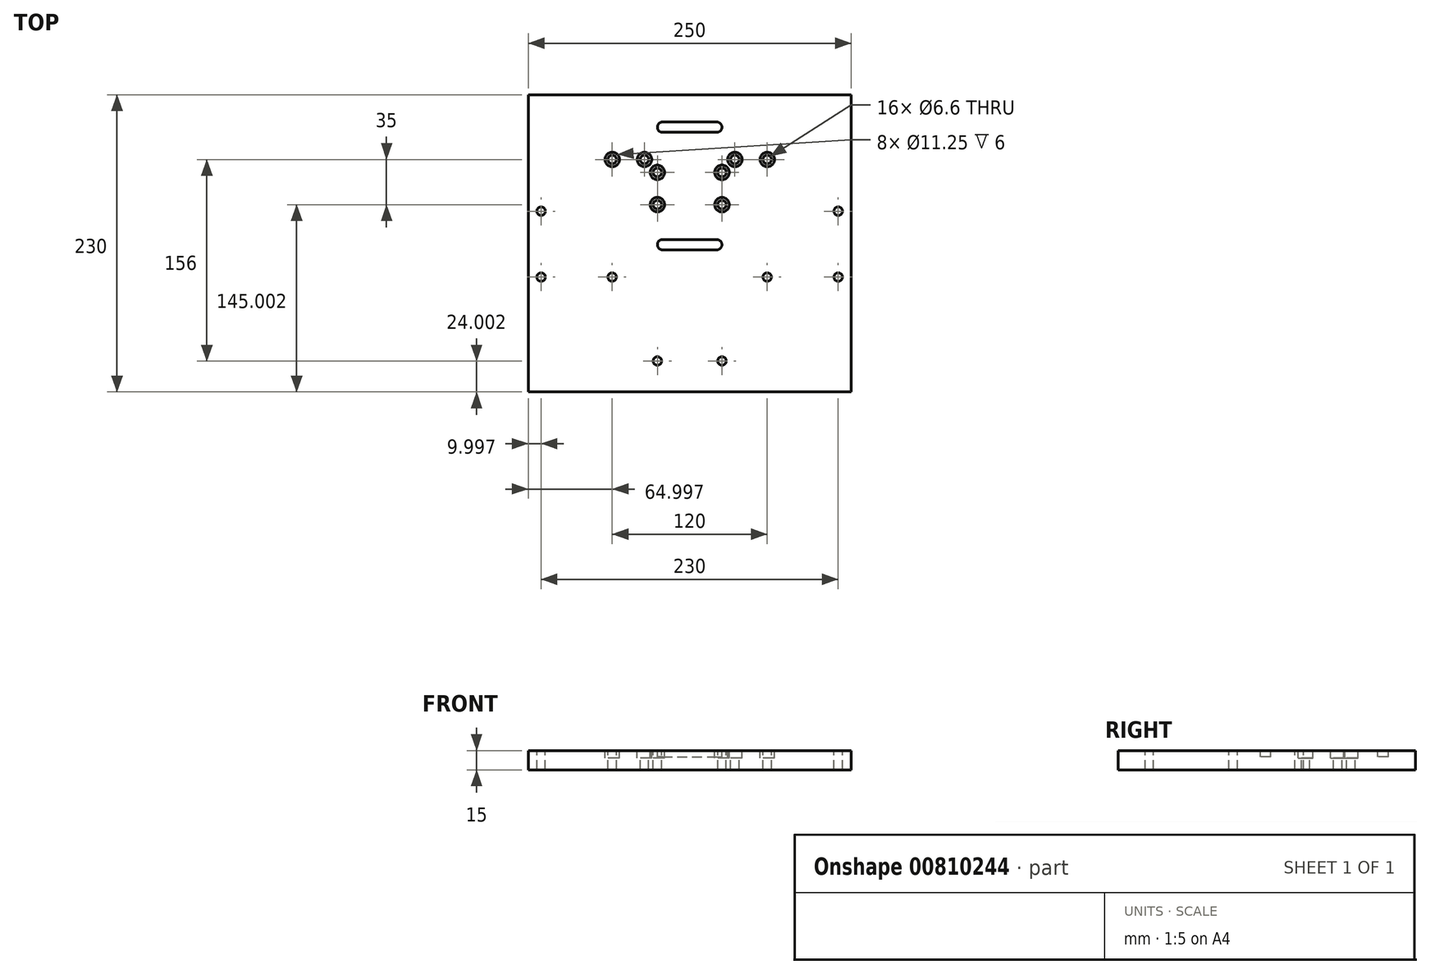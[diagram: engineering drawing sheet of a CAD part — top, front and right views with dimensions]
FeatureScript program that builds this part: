
annotation { "Feature Type Name" : "Feature", "Feature Type Description" : "" }
export const myFeature = defineFeature(function(context is Context, id is Id, definition is map)
    precondition{}
    {
        {
            var Q0;
            Q0=qCreatedBy(makeId("Top.planeOp"),FACE);
            var sketch = newSketch(context, id + "F0", { "sketchPlane" : qUnion([Q0])});
            skLineSegment(sketch, "E0.bottom", {"start": v(-186.98, -45.7) * mm, "end": v(63.02, -45.7) * mm});
            skLineSegment(sketch, "E0.top", {"start": v(-186.98, 184.3) * mm, "end": v(63.02, 184.3) * mm});
            skLineSegment(sketch, "E0.left", {"start": v(-186.98, -45.7) * mm, "end": v(-186.98, 184.3) * mm});
            skLineSegment(sketch, "E0.right", {"start": v(63.02, -45.7) * mm, "end": v(63.02, 184.3) * mm});
            skSolve(sketch);
        }
        {
            var Q0;
            Q0=makeQuery(id+"F0.imprint","IMPRINT",FACE,{"disambiguationData":[TD([[makeQuery(id+"F0.imprint","IMPRINT",EDGE,{"derivedFrom":sQuery(id+"F0.wireOp",EDGE,"E0.bottom")}),1.0]])]});
            extrude(context, id + "F1", {"entities" : qUnion([Q0]), "depth" : 15 * mm, "offsetDistance" : 25 * mm});
        }
        {
            var Q0;
            Q0=makeQuery(id+"F1.opExtrude","CAP_FACE",FACE,{"disambiguationData":[OSD([sQuery(id+"F0.wireOp",EDGE,"E0.bottom"),sQuery(id+"F0.wireOp",EDGE,"E0.top"),sQuery(id+"F0.wireOp",EDGE,"E0.left"),sQuery(id+"F0.wireOp",EDGE,"E0.right")])],"isStart":false});
            var sketch = newSketch(context, id + "F2", { "sketchPlane" : qUnion([Q0])});
            skLineSegment(sketch, "E1", {"start": v(-61.98, 184.3) * mm, "end": v(-61.98, -45.7) * mm});
            skCircle(sketch, "E2", {"center": v(-121.98, 134.3) * mm, "radius": 3 * mm});
            skCircle(sketch, "E3", {"center": v(-96.98, 134.3) * mm, "radius": 3 * mm});
            skCircle(sketch, "E4", {"center": v(-26.98, 134.3) * mm, "radius": 3 * mm});
            skCircle(sketch, "E5", {"center": v(-1.98, 134.3) * mm, "radius": 3 * mm});
            skCircle(sketch, "E6", {"center": v(-86.98, 124.3) * mm, "radius": 3 * mm});
            skCircle(sketch, "E7", {"center": v(-86.98, 99.3) * mm, "radius": 3 * mm});
            skCircle(sketch, "E8", {"center": v(-36.98, 124.3) * mm, "radius": 3 * mm});
            skCircle(sketch, "E9", {"center": v(-36.98, 99.3) * mm, "radius": 3 * mm});
            skLineSegment(sketch, "E10.bottom", {"start": v(-82.98, 72.3) * mm, "end": v(-40.98, 72.3) * mm});
            skLineSegment(sketch, "E10.top", {"start": v(-82.98, 64.3) * mm, "end": v(-40.98, 64.3) * mm});
            skLineSegment(sketch, "E10.left", {"start": v(-86.98, 68.3) * mm, "end": v(-86.98, 68.3) * mm});
            skLineSegment(sketch, "E10.right", {"start": v(-36.98, 68.3) * mm, "end": v(-36.98, 68.3) * mm});
            skPoint(sketch, "E10.middle", {"position": v(-61.98, 68.3) * mm});
            skPoint(sketch, "E11.visualSharp", {"position": v(-86.98, 72.3) * mm});
            skArc(sketch, "E11.filletArc", {"start": v(-82.98, 72.3) * mm, "mid": v(-85.81, 71.13) * mm, "end": v(-86.98, 68.3) * mm});
            skPoint(sketch, "E12.visualSharp", {"position": v(-86.98, 64.3) * mm});
            skArc(sketch, "E12.filletArc", {"start": v(-86.98, 68.3) * mm, "mid": v(-85.81, 65.47) * mm, "end": v(-82.98, 64.3) * mm});
            skPoint(sketch, "E13.visualSharp", {"position": v(-36.98, 72.3) * mm});
            skArc(sketch, "E13.filletArc", {"start": v(-36.98, 68.3) * mm, "mid": v(-38.15, 71.13) * mm, "end": v(-40.98, 72.3) * mm});
            skPoint(sketch, "E14.visualSharp", {"position": v(-36.98, 64.3) * mm});
            skArc(sketch, "E14.filletArc", {"start": v(-40.98, 64.3) * mm, "mid": v(-38.15, 65.47) * mm, "end": v(-36.98, 68.3) * mm});
            skCircle(sketch, "E15", {"center": v(-176.98, 94.3) * mm, "radius": 3 * mm});
            skCircle(sketch, "E16", {"center": v(53.02, 94.3) * mm, "radius": 3 * mm});
            skCircle(sketch, "E17", {"center": v(53.02, 43.3) * mm, "radius": 3 * mm});
            skCircle(sketch, "E18", {"center": v(-176.98, 43.3) * mm, "radius": 3 * mm});
            skCircle(sketch, "E19", {"center": v(-121.98, 43.3) * mm, "radius": 3 * mm});
            skCircle(sketch, "E20", {"center": v(-1.98, 43.3) * mm, "radius": 3 * mm});
            skCircle(sketch, "E21", {"center": v(-86.98, -21.7) * mm, "radius": 3 * mm});
            skCircle(sketch, "E22", {"center": v(-36.98, -21.7) * mm, "radius": 3 * mm});
            skLineSegment(sketch, "E23.bottom", {"start": v(-82.98, 163.3) * mm, "end": v(-40.98, 163.3) * mm});
            skLineSegment(sketch, "E23.top", {"start": v(-82.98, 155.3) * mm, "end": v(-40.98, 155.3) * mm});
            skLineSegment(sketch, "E23.left", {"start": v(-86.98, 159.3) * mm, "end": v(-86.98, 159.3) * mm});
            skLineSegment(sketch, "E23.right", {"start": v(-36.98, 159.3) * mm, "end": v(-36.98, 159.3) * mm});
            skPoint(sketch, "E23.middle", {"position": v(-61.98, 159.3) * mm});
            skPoint(sketch, "E24.visualSharp", {"position": v(-86.98, 163.3) * mm});
            skArc(sketch, "E24.filletArc", {"start": v(-82.98, 163.3) * mm, "mid": v(-85.81, 162.13) * mm, "end": v(-86.98, 159.3) * mm});
            skPoint(sketch, "E25.visualSharp", {"position": v(-86.98, 155.3) * mm});
            skArc(sketch, "E25.filletArc", {"start": v(-86.98, 159.3) * mm, "mid": v(-85.81, 156.47) * mm, "end": v(-82.98, 155.3) * mm});
            skPoint(sketch, "E26.visualSharp", {"position": v(-36.98, 163.3) * mm});
            skArc(sketch, "E26.filletArc", {"start": v(-36.98, 159.3) * mm, "mid": v(-38.15, 162.13) * mm, "end": v(-40.98, 163.3) * mm});
            skPoint(sketch, "E27.visualSharp", {"position": v(-36.98, 155.3) * mm});
            skArc(sketch, "E27.filletArc", {"start": v(-40.98, 155.3) * mm, "mid": v(-38.15, 156.47) * mm, "end": v(-36.98, 159.3) * mm});
            skSolve(sketch);
        }
        {
            var Q0;
            Q0=sQuery(id+"F2.wireOp",VERTEX,"E2.center");
            var Q1;
            Q1=sQuery(id+"F2.wireOp",VERTEX,"E3.center");
            var Q2;
            Q2=sQuery(id+"F2.wireOp",VERTEX,"E6.center");
            var Q3;
            Q3=sQuery(id+"F2.wireOp",VERTEX,"E7.center");
            var Q4;
            Q4=sQuery(id+"F2.wireOp",VERTEX,"E9.center");
            var Q5;
            Q5=sQuery(id+"F2.wireOp",VERTEX,"E8.center");
            var Q6;
            Q6=sQuery(id+"F2.wireOp",VERTEX,"E4.center");
            var Q7;
            Q7=sQuery(id+"F2.wireOp",VERTEX,"E5.center");
            var Q8;
            Q8=makeQuery(id+"F1.opExtrude","SWEPT_BODY",BODY,{"disambiguationData":[OSD([sQuery(id+"F0.wireOp",EDGE,"E0.bottom"),sQuery(id+"F0.wireOp",EDGE,"E0.top"),sQuery(id+"F0.wireOp",EDGE,"E0.left"),sQuery(id+"F0.wireOp",EDGE,"E0.right")])]});
            hole(context, id + "F3", {"style" : HoleStyle.C_BORE, "endStyle" : HoleEndStyle.THROUGH, "standardTappedOrClearance" : lookupTablePath({ "standard" : "ISO", "fit" : "Normal", "size" : "M6", "type" : "Clearance" }), "standardBlindInLast" : lookupTablePath({ "fit" : "Standard", "standard" : "ISO", "size" : "M6", "type" : "Clearance" }), "holeDiameter" : 6.6 * mm, "cBoreDiameter" : 11.25 * mm, "cBoreDepth" : 6 * mm, "majorDiameter" : 5 * mm, "isTappedThrough" : true, "tappedDepth" : 12 * mm, "tapClearance" : 3, "startFromSketch" : true, "locations" : qUnion([Q0, Q1, Q2, Q3, Q4, Q5, Q6, Q7]), "scope" : qUnion([Q8])});
        }
        {
            var Q0;
            {var subQ4=sQuery(id+"F2.wireOp",EDGE,"E13.filletArc");Q0=makeQuery(id+"F2.imprint","IMPRINT",FACE,{"disambiguationData":[TD([[makeQuery(id+"F2.imprint","IMPRINT",EDGE,{"derivedFrom":subQ4}),1.0]])]});}
            var Q1;
            {var subQ0=sQuery(id+"F2.wireOp",EDGE,"E11.filletArc");Q1=makeQuery(id+"F2.imprint","IMPRINT",FACE,{"disambiguationData":[TD([[makeQuery(id+"F2.imprint","IMPRINT",EDGE,{"derivedFrom":subQ0}),1.0]])]});}
            extrude(context, id + "F4", {"entities" : qUnion([Q0, Q1]), "operationType" : NewBodyOperationType.REMOVE, "oppositeDirection" : true, "depth" : 5 * mm, "offsetDistance" : 25 * mm});
        }
        {
            var Q0;
            Q0=sQuery(id+"F2.wireOp",VERTEX,"E17.center");
            var Q1;
            Q1=sQuery(id+"F2.wireOp",VERTEX,"E20.center");
            var Q2;
            Q2=sQuery(id+"F2.wireOp",VERTEX,"E16.center");
            var Q3;
            Q3=sQuery(id+"F2.wireOp",VERTEX,"E22.center");
            var Q4;
            Q4=sQuery(id+"F2.wireOp",VERTEX,"E21.center");
            var Q5;
            Q5=sQuery(id+"F2.wireOp",VERTEX,"E19.center");
            var Q6;
            Q6=sQuery(id+"F2.wireOp",VERTEX,"E18.center");
            var Q7;
            Q7=sQuery(id+"F2.wireOp",VERTEX,"E15.center");
            var Q8;
            Q8=makeQuery(id+"F1.opExtrude","SWEPT_BODY",BODY,{"disambiguationData":[OSD([sQuery(id+"F0.wireOp",EDGE,"E0.bottom"),sQuery(id+"F0.wireOp",EDGE,"E0.top"),sQuery(id+"F0.wireOp",EDGE,"E0.left"),sQuery(id+"F0.wireOp",EDGE,"E0.right")])]});
            hole(context, id + "F5", {"style" : HoleStyle.SIMPLE, "endStyle" : HoleEndStyle.THROUGH, "standardTappedOrClearance" : lookupTablePath({ "standard" : "ISO", "fit" : "Normal", "size" : "M6", "type" : "Clearance" }), "standardBlindInLast" : lookupTablePath({ "fit" : "Standard", "standard" : "ISO", "size" : "M6", "type" : "Clearance" }), "holeDiameter" : 6.6 * mm, "majorDiameter" : 5 * mm, "isTappedThrough" : true, "tappedDepth" : 12 * mm, "tapClearance" : 3, "startFromSketch" : true, "locations" : qUnion([Q0, Q1, Q2, Q3, Q4, Q5, Q6, Q7]), "scope" : qUnion([Q8])});
        }
        {
            var Q0;
            {var subQ0=sQuery(id+"F2.wireOp",EDGE,"E24.filletArc");Q0=makeQuery(id+"F2.imprint","IMPRINT",FACE,{"disambiguationData":[TD([[makeQuery(id+"F2.imprint","IMPRINT",EDGE,{"derivedFrom":subQ0}),1.0]])]});}
            var Q1;
            {var subQ4=sQuery(id+"F2.wireOp",EDGE,"E26.filletArc");Q1=makeQuery(id+"F2.imprint","IMPRINT",FACE,{"disambiguationData":[TD([[makeQuery(id+"F2.imprint","IMPRINT",EDGE,{"derivedFrom":subQ4}),1.0]])]});}
            extrude(context, id + "F6", {"entities" : qUnion([Q0, Q1]), "operationType" : NewBodyOperationType.REMOVE, "oppositeDirection" : true, "depth" : 5 * mm, "offsetDistance" : 25 * mm});
        }
    });
